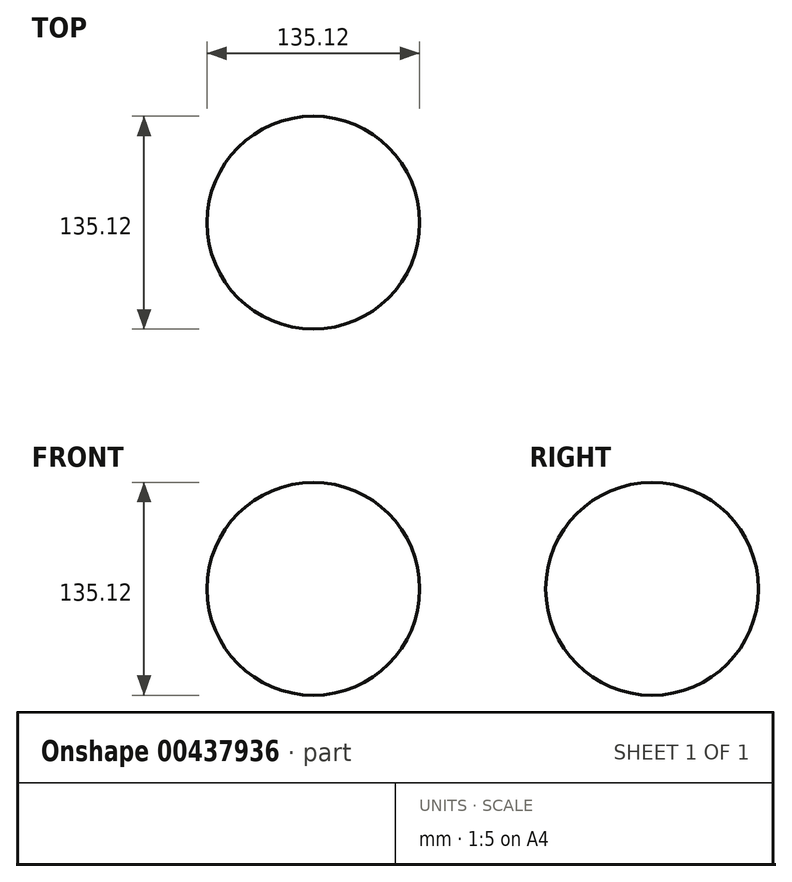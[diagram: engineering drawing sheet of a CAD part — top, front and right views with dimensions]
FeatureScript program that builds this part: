
annotation { "Feature Type Name" : "Feature", "Feature Type Description" : "" }
export const myFeature = defineFeature(function(context is Context, id is Id, definition is map)
    precondition{}
    {
        {
            var Q0;
            Q0=qCreatedBy(makeId("Right.planeOp"),FACE);
            var sketch = newSketch(context, id + "F0", { "sketchPlane" : qUnion([Q0])});
            skCircle(sketch, "E0", {"center": v(0, -2.29) * mm, "radius": 67.56 * mm});
            skLineSegment(sketch, "E1", {"start": v(0, 65.27) * mm, "end": v(0, -69.85) * mm});
            skSolve(sketch);
        }
        {
            var Q0;
            {var subQ0=sQuery(id+"F0.wireOp",EDGE,"E1");Q0=makeQuery(id+"F0.imprint","IMPRINT",FACE,{"disambiguationData":[TD([[makeQuery(id+"F0.imprint","IMPRINT",EDGE,{"derivedFrom":subQ0}),-1.0]])]});}
            var Q1;
            Q1=sQuery(id+"F0.wireOp",EDGE,"E1");
            revolve(context, id + "F1", {"entities" : qUnion([Q0]), "axis" : qUnion([Q1]), "revolveType" : RevolveType.FULL});
        }
    });
